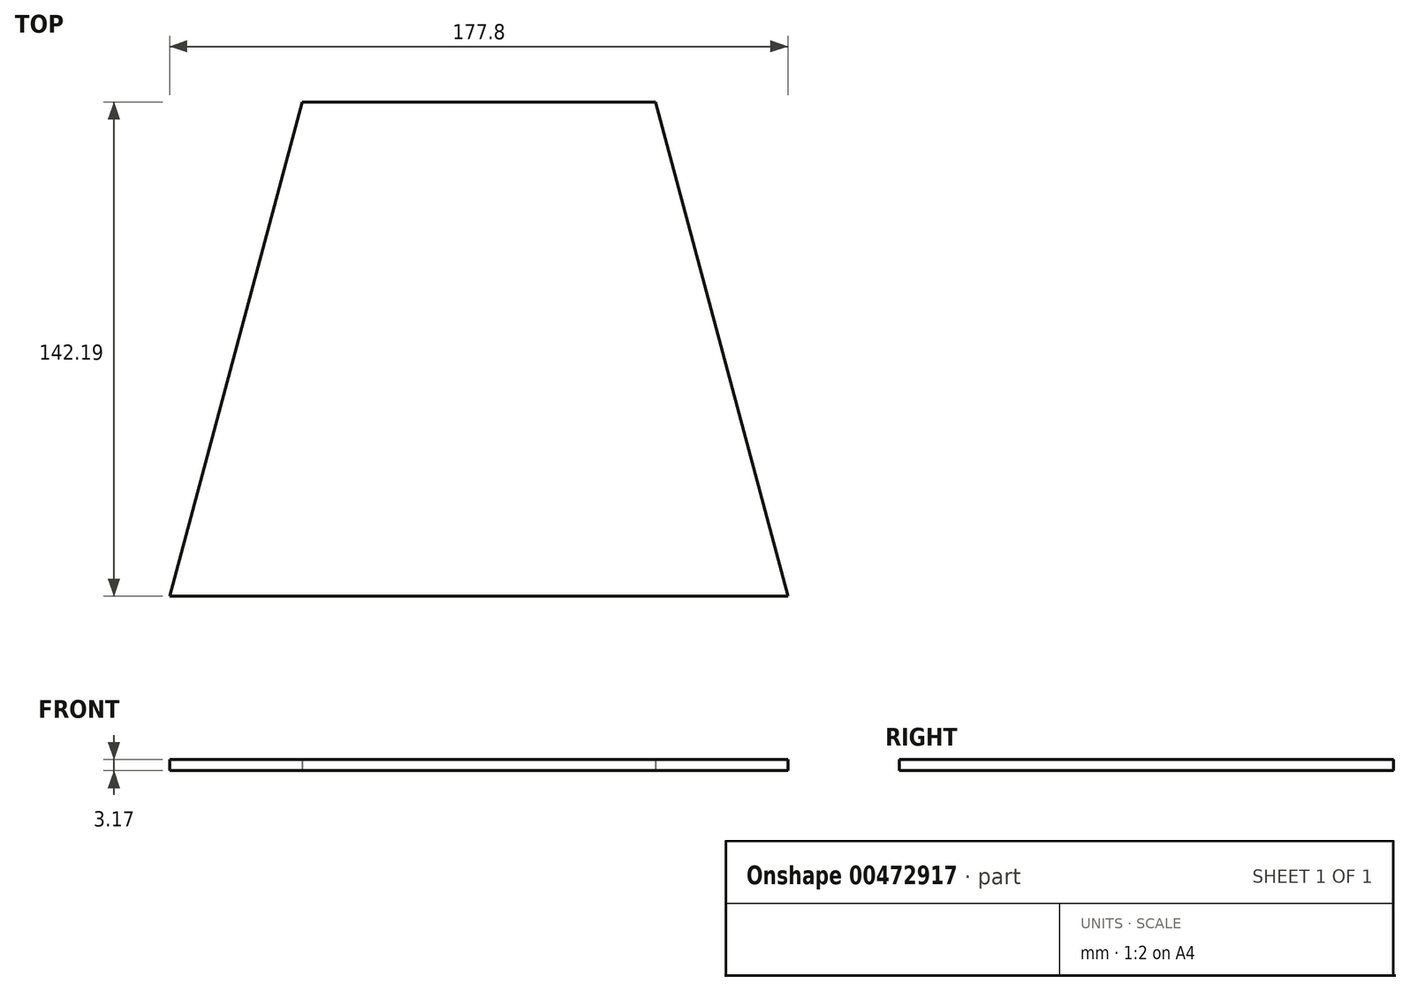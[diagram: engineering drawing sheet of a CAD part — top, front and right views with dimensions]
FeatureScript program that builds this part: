
annotation { "Feature Type Name" : "Feature", "Feature Type Description" : "" }
export const myFeature = defineFeature(function(context is Context, id is Id, definition is map)
    precondition{}
    {
        {
            var Q0;
            Q0=qCreatedBy(makeId("Top.planeOp"),FACE);
            var sketch = newSketch(context, id + "F0", { "sketchPlane" : qUnion([Q0])});
            skLineSegment(sketch, "E0", {"start": v(-88.9, 0) * mm, "end": v(88.9, 0) * mm});
            skLineSegment(sketch, "E1", {"start": v(88.9, 0) * mm, "end": v(50.8, 142.2) * mm});
            skLineSegment(sketch, "E2", {"start": v(50.8, 142.2) * mm, "end": v(-50.8, 142.2) * mm});
            skLineSegment(sketch, "E3", {"start": v(-50.8, 142.2) * mm, "end": v(-88.9, 0) * mm});
            skLineSegment(sketch, "E4", {"start": v(0, 142.2) * mm, "end": v(0, 0) * mm, "construction": true});
            skPoint(sketch, "E4.endSnap0", {"position": v(0, 0) * mm});
            skSolve(sketch);
        }
        {
            var Q0;
            Q0 = qSketchRegion(id + "F0", true);
            extrude(context, id + "F1", {"entities" : qUnion([Q0]), "depth" : 3.17 * mm});
        }
    });
